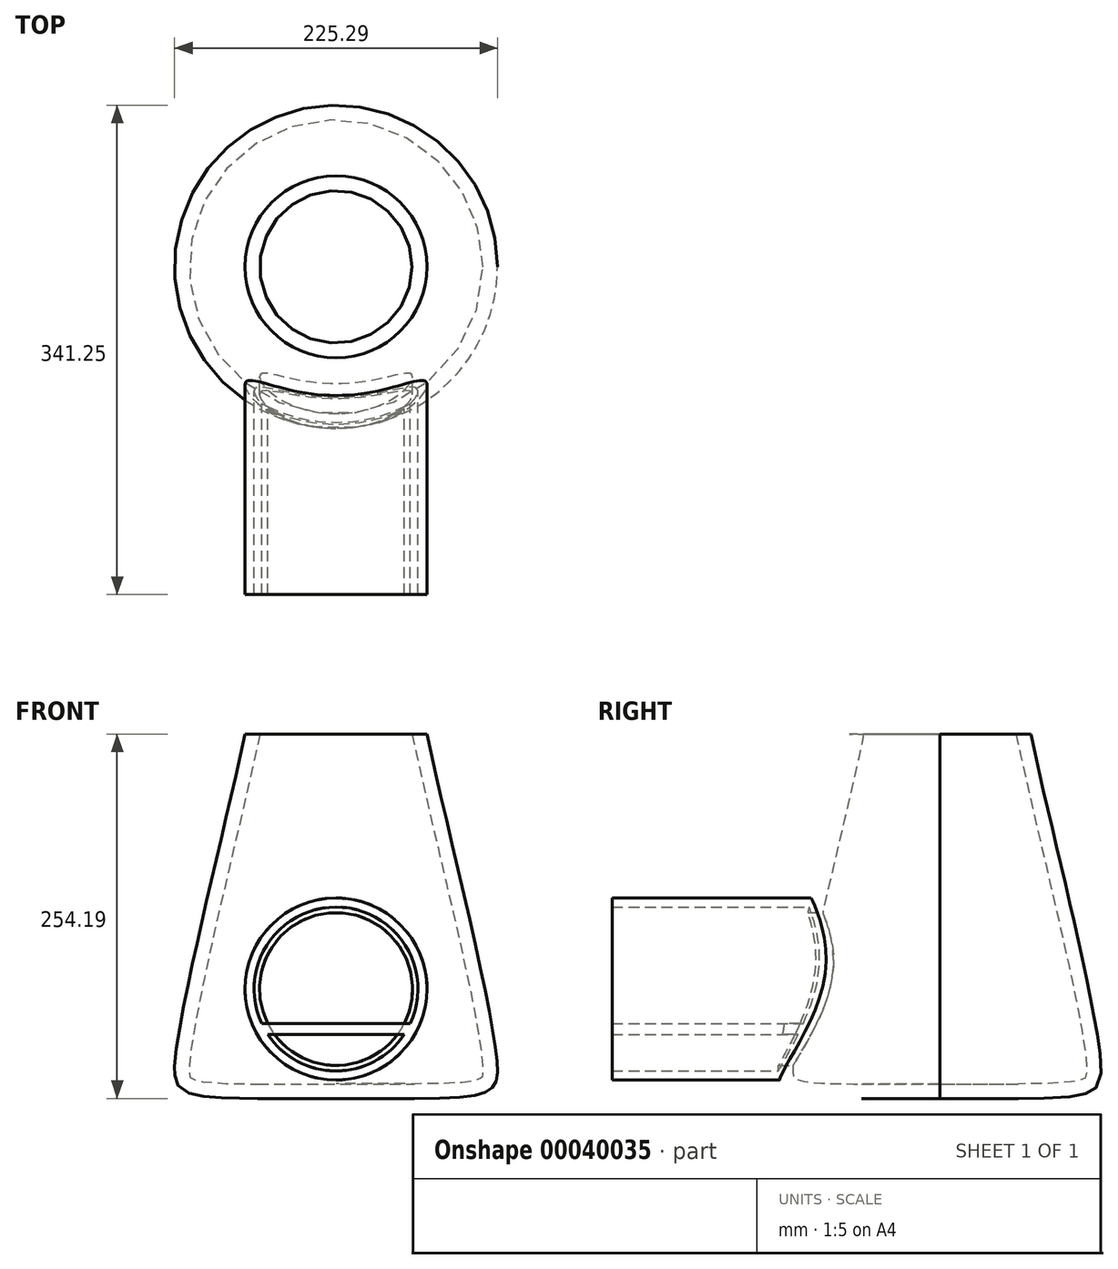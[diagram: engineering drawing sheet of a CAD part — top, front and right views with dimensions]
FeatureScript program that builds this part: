
annotation { "Feature Type Name" : "Feature", "Feature Type Description" : "" }
export const myFeature = defineFeature(function(context is Context, id is Id, definition is map)
    precondition{}
    {
        {
            var Q0;
            Q0=qCreatedBy(makeId("Front.planeOp"),FACE);
            var sketch = newSketch(context, id + "F0", { "sketchPlane" : qUnion([Q0])});
            skLineSegment(sketch, "E0", {"start": v(0, 0) * mm, "end": v(0, 254) * mm});
            skLineSegment(sketch, "E1", {"start": v(0, 254) * mm, "end": v(63.5, 254) * mm});
            skLineSegment(sketch, "E2", {"start": v(63.5, 254) * mm, "end": v(63.5, 254) * mm});
            skLineSegment(sketch, "E3.trimOffspring", {"start": v(69.66, 226.03) * mm, "end": v(69.66, 226.03) * mm});
            skFitSpline(sketch, "E4.trimOffspring", {"points": [v(63.5, 254) * mm, v(112.1, 28.18) * mm, v(0, 0) * mm], "startDerivative": vector(64.98, -310.02) * mm, "endDerivative": vector(-766.51, 0) * mm});
            skSolve(sketch);
        }
        {
            var Q0;
            Q0=makeQuery(id+"F0.imprint","IMPRINT",FACE,{"disambiguationData":[TD([[makeQuery(id+"F0.imprint","IMPRINT",EDGE,{"derivedFrom":sQuery(id+"F0.wireOp",EDGE,"E0")}),-1.0]])]});
            var Q1;
            Q1=sQuery(id+"F0.wireOp",EDGE,"E0");
            revolve(context, id + "F1", {"entities" : qUnion([Q0]), "axis" : qUnion([Q1]), "revolveType" : RevolveType.FULL});
        }
        {
            var Q0;
            Q0=qCreatedBy(makeId("Front.planeOp"),FACE);
            var sketch = newSketch(context, id + "F2", { "sketchPlane" : qUnion([Q0])});
            skCircle(sketch, "E5", {"center": v(0, 76.2) * mm, "radius": 63.5 * mm});
            skCircle(sketch, "E6", {"center": v(0, 76.2) * mm, "radius": 57.15 * mm});
            skLineSegment(sketch, "E7", {"start": v(51.8, 52.07) * mm, "end": v(-51.8, 52.07) * mm});
            skLineSegment(sketch, "E8", {"start": v(47.52, 44.45) * mm, "end": v(-47.52, 44.45) * mm});
            skSolve(sketch);
        }
        {
            var Q0;
            Q0 = qSketchRegion(id + "F2", true);
            var Q1;
            {var subQ0=sQuery(id+"F2.wireOp",EDGE,"E7");Q1=makeQuery(id+"F2.imprint","IMPRINT",FACE,{"disambiguationData":[TD([[makeQuery(id+"F2.imprint","IMPRINT",EDGE,{"derivedFrom":subQ0}),1.0]])]});}
            extrude(context, id + "F3", {"entities" : qUnion([Q0, Q1]), "operationType" : NewBodyOperationType.ADD, "depth" : 228.6 * mm});
        }
        {
            var Q0;
            {var subQ0=sQuery(id+"F2.wireOp",EDGE,"E7");Q0=makeQuery(id+"F3.boolean.opBoolean","SPLIT",FACE,{"disambiguationData":[TD([makeQuery(id+"F3.opExtrude","SWEPT_FACE",FACE,{"disambiguationData":[OSD([subQ0])]})])],"derivedFrom":makeQuery(id+"F1.opRevolve","SWEPT_FACE",FACE,{"disambiguationData":[OSD([sQuery(id+"F0.wireOp",EDGE,"E4.trimOffspring")])]})});}
            var Q1;
            {var subQ0=sQuery(id+"F2.wireOp",EDGE,"E8");Q1=makeQuery(id+"F3.boolean.opBoolean","SPLIT",FACE,{"disambiguationData":[TD([makeQuery(id+"F3.opExtrude","SWEPT_FACE",FACE,{"disambiguationData":[OSD([subQ0])]})])],"derivedFrom":makeQuery(id+"F1.opRevolve","SWEPT_FACE",FACE,{"disambiguationData":[OSD([sQuery(id+"F0.wireOp",EDGE,"E4.trimOffspring")])]})});}
            var Q2;
            Q2=makeQuery(id+"F1.opRevolve","SWEPT_FACE",FACE,{"disambiguationData":[OSD([sQuery(id+"F0.wireOp",EDGE,"E1")])]});
            shell(context, id + "F4", {"entities" : qUnion([Q0, Q1, Q2]), "thickness" : 10.16 * mm});
        }
    });
